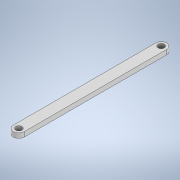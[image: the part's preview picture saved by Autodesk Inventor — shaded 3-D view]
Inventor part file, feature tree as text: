
AUTODESK INVENTOR PART (.ipt)
format: ipt  version: 2020 (Build 240168000, 168)  size: 109,056 bytes
history: native  units: in
note: dims shown in document units (in); Inventor stores cm internally (conversion verified against a paired STEP export)
features: extrude x2, sketch x2
ambient origin geometry x8: Origin, YZ Plane, XZ Plane, XY Plane, X Axis, Y Axis, Z Axis, Center Point
bodies: Solid1 (feature_tree)
feature tree (4):
  extrude  "Extrusion1"  Depth=0.2756in
  extrude  "Extrusion2"  Depth=3.5433in
  sketch  "Sketch1"  dims[d0=0.2756in d1=0.2756in]
  sketch  "Sketch2"  dims[d2=0.1181in d3=0.0in d4=0.1575in d5=0.1575in d7=0.1181in d8=0.0in d9=3.5433in]
